# Revit family: Eyewash-Bradley_Corp-Wall_Drop_Down-S19274HWB
name_source: partatom
category: Plumbing Fixtures
units: mm (PartAtom-declared; Revit-internal decimal feet)

## family parameters
Cut with Voids When Loaded = No
Host = Face
Maintain Annotation Orientation = No
OmniClass Number = 23.65.00.00
OmniClass Title = Supply and Distribution of Liquids and Gases
Part Type = Normal
Room Calculation Point = No
Round Connector Dimension = Use Radius
Shared = No

## types (1)
- S19274HWB
    Assembly Code = D2010710
    Barrier-Free = No
    Buy American Act = TBD
    CWFU = 0
    Cold Water Connection Diameter = 1"
    Cold Water Connection Radius = 0"
    Default Elevation = 36"
    Description = Wall-Mount Swing-Down Halo Eyewash Unit
    Fixture Material = Metal - Bradley Corp - Chrome
    Height = 7"
    Industry Standards = ANSI Z358.1-2009, cUPC
    Length = 11"
    Manufacturer = Bradley Corporation
    Manufacturer Installation URL - English = https://www.bradleycorp.com
    MasterFormat Number = 22.45.26
    MasterFormat Title = Eye/Face Wash Equipment
    Model = S19274HWB
    Mounting Height = 0"
    Navigator EFX8 Emergency Thermostatic Mixing Valve = No
    Percentage of Recycled Content = 0
    Pipe Fitting Material = Metal - Bradley Corp - Chrome
    Product Page URL = https://www.bradleycorp.com
    Product Tech Data URL - English = https://www.bradleycorp.com
    Product Tech Data URL - Spanish = https://www.bradleycorp.com
    Specifications URL = https://www.bradleycorp.com
    URL = http://www.bradleycorp.com
    Version = 1.0
    WFU = 0
    Warranty Information = Full, One-Year Warranty
    Waste Connection Radius = 1"
    Width = 7 5/8"

## geometry (parser evidence)
native form markers: Blend x14, Sweep x3
no freeform markers — native parametric forms only
